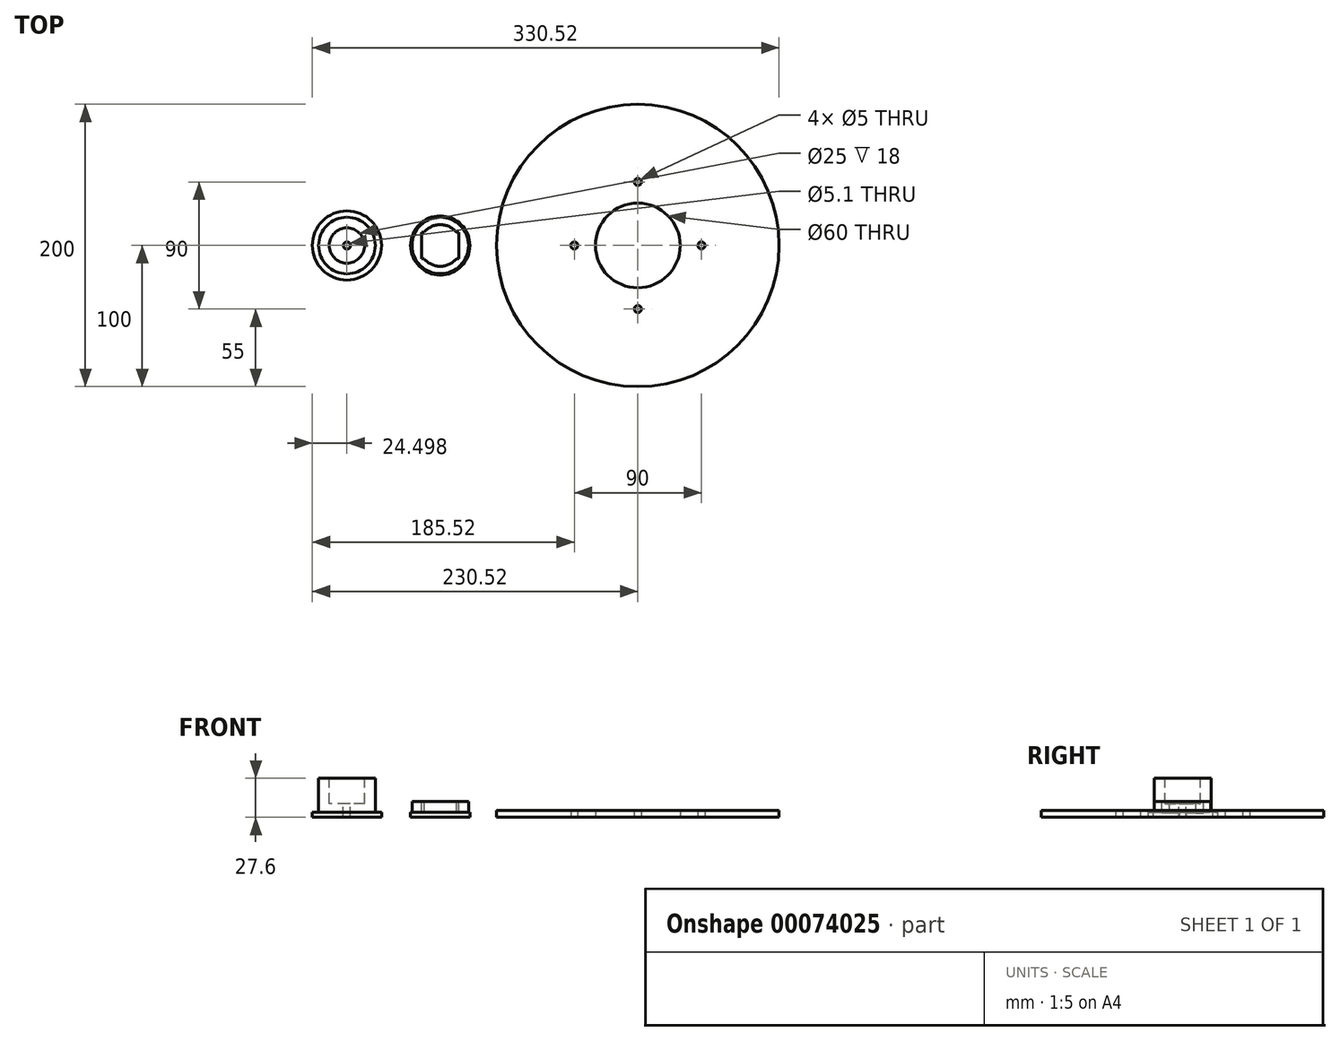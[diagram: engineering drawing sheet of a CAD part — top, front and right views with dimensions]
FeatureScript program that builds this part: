
annotation { "Feature Type Name" : "Feature", "Feature Type Description" : "" }
export const myFeature = defineFeature(function(context is Context, id is Id, definition is map)
    precondition{}
    {
        {
            var Q0;
            Q0=qCreatedBy(makeId("Top.planeOp"),FACE);
            var sketch = newSketch(context, id + "F0", { "sketchPlane" : qUnion([Q0])});
            skCircle(sketch, "E0", {"center": v(0, 0) * mm, "radius": 100 * mm});
            skCircle(sketch, "E1", {"center": v(0, 0) * mm, "radius": 30 * mm});
            skPoint(sketch, "E2", {"position": v(-45, 0) * mm});
            skCircle(sketch, "E3", {"center": v(-45, 0) * mm, "radius": 2.5 * mm});
            skCircle(sketch, "E4.1.0", {"center": v(0, -45) * mm, "radius": 2.5 * mm});
            skCircle(sketch, "E4.2.0", {"center": v(45, 0) * mm, "radius": 2.5 * mm});
            skCircle(sketch, "E4.3.0", {"center": v(0, 45) * mm, "radius": 2.5 * mm});
            skSolve(sketch);
        }
        {
            var Q0;
            Q0=makeQuery(id+"F0.imprint","IMPRINT",FACE,{"disambiguationData":[TD([[makeQuery(id+"F0.imprint","IMPRINT",EDGE,{"derivedFrom":sQuery(id+"F0.wireOp",EDGE,"E0")}),1.0]])]});
            extrude(context, id + "F1", {"entities" : qUnion([Q0]), "depth" : 5 * mm, "offsetDistance" : 25 * mm});
        }
        {
            var Q0;
            Q0=qCreatedBy(makeId("Top.planeOp"),FACE);
            var sketch = newSketch(context, id + "F2", { "sketchPlane" : qUnion([Q0])});
            skCircle(sketch, "E5", {"center": v(-206.02, 0) * mm, "radius": 24.5 * mm});
            skSolve(sketch);
        }
        {
            var Q0;
            Q0=makeQuery(id+"F2.imprint","IMPRINT",FACE,{"disambiguationData":[TD([[makeQuery(id+"F2.imprint","IMPRINT",EDGE,{"derivedFrom":sQuery(id+"F2.wireOp",EDGE,"E5")}),1.0]])]});
            extrude(context, id + "F3", {"entities" : qUnion([Q0]), "depth" : 3.6 * mm, "offsetDistance" : 25 * mm});
        }
        {
            var Q0;
            Q0=makeQuery(id+"F3.opExtrude","CAP_FACE",FACE,{"disambiguationData":[OSD([sQuery(id+"F2.wireOp",EDGE,"E5")])],"isStart":false});
            var sketch = newSketch(context, id + "F4", { "sketchPlane" : qUnion([Q0])});
            skCircle(sketch, "E6", {"center": v(-206.02, 0) * mm, "radius": 20.05 * mm});
            skSolve(sketch);
        }
        {
            var Q0;
            Q0 = qSketchRegion(id + "F4", true);
            extrude(context, id + "F5", {"entities" : qUnion([Q0]), "operationType" : NewBodyOperationType.ADD, "depth" : 24 * mm, "offsetDistance" : 25 * mm});
        }
        {
            var Q0;
            Q0=makeQuery(id+"F5.opExtrude","CAP_FACE",FACE,{"disambiguationData":[OSD([sQuery(id+"F4.wireOp",EDGE,"E6")])],"isStart":false});
            var sketch = newSketch(context, id + "F6", { "sketchPlane" : qUnion([Q0])});
            skCircle(sketch, "E7", {"center": v(-206.02, 0) * mm, "radius": 12.5 * mm});
            skSolve(sketch);
        }
        {
            var Q0;
            Q0 = qSketchRegion(id + "F6", true);
            extrude(context, id + "F7", {"entities" : qUnion([Q0]), "operationType" : NewBodyOperationType.REMOVE, "oppositeDirection" : true, "depth" : 18 * mm, "offsetDistance" : 25 * mm});
        }
        {
            var Q0;
            Q0=makeQuery(id+"F7.boolean.opBoolean","COPY",FACE,{"derivedFrom":makeQuery(id+"F7.opExtrude","CAP_FACE",FACE,{"disambiguationData":[OSD([sQuery(id+"F6.wireOp",EDGE,"E7")])],"isStart":false})});
            var sketch = newSketch(context, id + "F8", { "sketchPlane" : qUnion([Q0])});
            skPoint(sketch, "E8", {"position": v(-206.02, 0) * mm});
            skSolve(sketch);
        }
        {
            var Q0;
            Q0=sQuery(id+"F8.wireOp",VERTEX,"E8");
            var Q1;
            Q1=makeQuery(id+"F3.opExtrude","SWEPT_BODY",BODY,{"disambiguationData":[OSD([sQuery(id+"F2.wireOp",EDGE,"E5")])]});
            hole(context, id + "F9", {"style" : HoleStyle.SIMPLE, "endStyle" : HoleEndStyle.THROUGH, "holeDiameter" : 5.1 * mm, "majorDiameter" : 5 * mm, "tappedDepth" : 12 * mm, "tapClearance" : 3, "locations" : qUnion([Q0]), "scope" : qUnion([Q1])});
        }
        {
            var Q0;
            Q0=qCreatedBy(makeId("Top.planeOp"),FACE);
            var sketch = newSketch(context, id + "F10", { "sketchPlane" : qUnion([Q0])});
            skCircle(sketch, "E9", {"center": v(-139.9, 0) * mm, "radius": 21 * mm});
            skSolve(sketch);
        }
        {
            var Q0;
            Q0=makeQuery(id+"F10.imprint","IMPRINT",FACE,{"disambiguationData":[TD([[makeQuery(id+"F10.imprint","IMPRINT",EDGE,{"derivedFrom":sQuery(id+"F10.wireOp",EDGE,"E9")}),1.0]])]});
            extrude(context, id + "F11", {"entities" : qUnion([Q0]), "depth" : 3.6 * mm, "offsetDistance" : 25 * mm});
        }
        {
            var Q0;
            Q0=makeQuery(id+"F11.opExtrude","CAP_FACE",FACE,{"disambiguationData":[OSD([sQuery(id+"F10.wireOp",EDGE,"E9")])],"isStart":false});
            var sketch = newSketch(context, id + "F12", { "sketchPlane" : qUnion([Q0])});
            skCircle(sketch, "E10", {"center": v(-139.9, 0) * mm, "radius": 20 * mm});
            skSolve(sketch);
        }
        {
            var Q0;
            Q0=makeQuery(id+"F12.imprint","IMPRINT",FACE,{"disambiguationData":[TD([[makeQuery(id+"F12.imprint","IMPRINT",EDGE,{"derivedFrom":sQuery(id+"F12.wireOp",EDGE,"E10")}),1.0]])]});
            extrude(context, id + "F13", {"entities" : qUnion([Q0]), "operationType" : NewBodyOperationType.ADD, "depth" : 7.5 * mm, "offsetDistance" : 25 * mm});
        }
        {
            var Q0;
            Q0=makeQuery(id+"F13.opExtrude","CAP_FACE",FACE,{"disambiguationData":[OSD([sQuery(id+"F12.wireOp",EDGE,"E10")])],"isStart":false});
            var sketch = newSketch(context, id + "F14", { "sketchPlane" : qUnion([Q0])});
            skArc(sketch, "E11", {"start": v(-128.5, 9.35) * mm, "mid": v(-139.9, 14.75) * mm, "end": v(-151.31, 9.35) * mm});
            skLineSegment(sketch, "E12.bottom", {"start": v(-126.65, 9.35) * mm, "end": v(-128.5, 9.35) * mm});
            skLineSegment(sketch, "E12.top", {"start": v(-126.65, -9.35) * mm, "end": v(-128.5, -9.35) * mm});
            skLineSegment(sketch, "E12.left", {"start": v(-126.65, 9.35) * mm, "end": v(-126.65, -9.35) * mm});
            skLineSegment(sketch, "E12.right", {"start": v(-153.15, 9.35) * mm, "end": v(-153.15, -9.35) * mm});
            skLineSegment(sketch, "E13.trimOffspring", {"start": v(-151.31, 9.35) * mm, "end": v(-153.15, 9.35) * mm});
            skArc(sketch, "E14.trimOffspring", {"start": v(-153.15, 6.48) * mm, "mid": v(-154.65, 0) * mm, "end": v(-153.15, -6.48) * mm});
            skArc(sketch, "E15.trimOffspring", {"start": v(-151.31, -9.35) * mm, "mid": v(-139.9, -14.75) * mm, "end": v(-128.5, -9.35) * mm});
            skLineSegment(sketch, "E16.trimOffspring", {"start": v(-151.31, -9.35) * mm, "end": v(-153.15, -9.35) * mm});
            skArc(sketch, "E17.trimOffspring", {"start": v(-126.65, -6.48) * mm, "mid": v(-125.15, 0) * mm, "end": v(-126.65, 6.48) * mm});
            skSolve(sketch);
        }
        {
            var Q0;
            Q0=makeQuery(id+"F14.imprint","IMPRINT",FACE,{"disambiguationData":[TD([[makeQuery(id+"F14.imprint","IMPRINT",EDGE,{"derivedFrom":sQuery(id+"F14.wireOp",EDGE,"E11")}),1.0]])]});
            extrude(context, id + "F15", {"entities" : qUnion([Q0]), "operationType" : NewBodyOperationType.REMOVE, "oppositeDirection" : true, "depth" : 8 * mm, "offsetDistance" : 25 * mm});
        }
        {
            var Q0;
            Q0=makeQuery(id+"F11.opExtrude","SWEPT_BODY",BODY,{"disambiguationData":[OSD([sQuery(id+"F10.wireOp",EDGE,"E9")])]});
            transform(context, id + "F16", {"entities" : qUnion([Q0]), "transformType" : TransformType.TRANSLATION_3D, "dx" : 0 * mm, "dy" : 0 * mm, "dz" : 0 * mm, "makeCopy" : true});
        }
        {
            var Q0;
            Q0=makeQuery(id+"F16.opPattern","COPY",BODY,{"derivedFrom":makeQuery(id+"F11.opExtrude","SWEPT_BODY",BODY,{"disambiguationData":[OSD([sQuery(id+"F10.wireOp",EDGE,"E9")])]}),"instanceName":"1"});
            deleteBodies(context, id + "F17", {"entities" : qUnion([Q0])});
        }
    });
